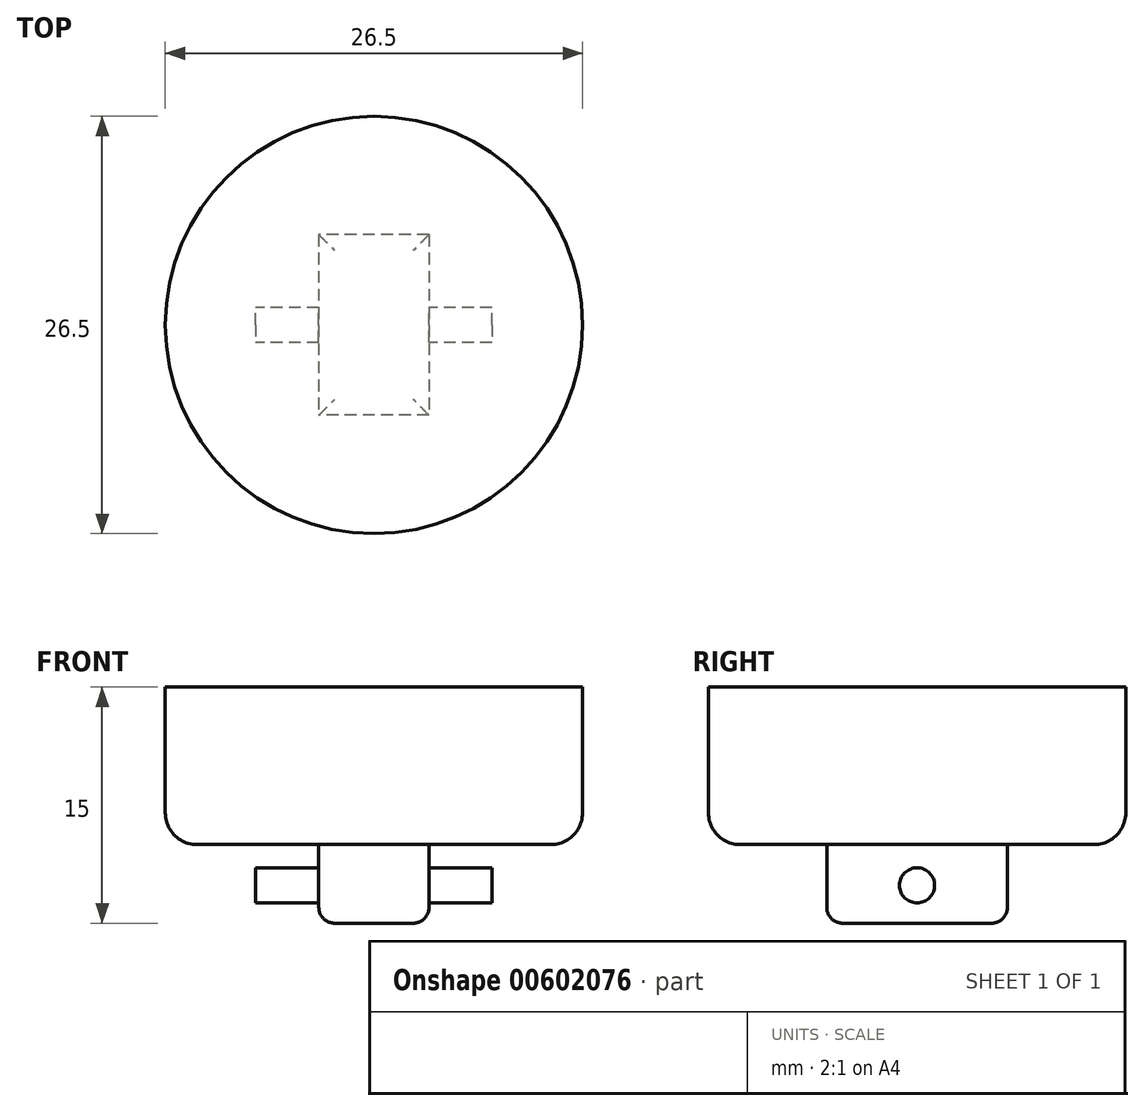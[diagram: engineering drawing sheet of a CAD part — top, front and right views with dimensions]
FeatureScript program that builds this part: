
annotation { "Feature Type Name" : "Feature", "Feature Type Description" : "" }
export const myFeature = defineFeature(function(context is Context, id is Id, definition is map)
    precondition{}
    {
        {
            var Q0;
            Q0=qCreatedBy(makeId("Top.planeOp"),FACE);
            var sketch = newSketch(context, id + "F0", { "sketchPlane" : qUnion([Q0])});
            skCircle(sketch, "E0", {"center": v(0, 0) * mm, "radius": 13.25 * mm});
            skSolve(sketch);
        }
        {
            var Q0;
            Q0 = qSketchRegion(id + "F0", true);
            extrude(context, id + "F1", {"entities" : qUnion([Q0]), "depth" : 10 * mm, "offsetDistance" : 25 * mm});
        }
        {
            var Q0;
            Q0=makeQuery(id+"F1.opExtrude","CAP_FACE",FACE,{"disambiguationData":[OSD([sQuery(id+"F0.wireOp",EDGE,"E0")])],"isStart":true});
            var sketch = newSketch(context, id + "F2", { "sketchPlane" : qUnion([Q0])});
            skLineSegment(sketch, "E1.bottom", {"start": v(3.5, -5.73) * mm, "end": v(-3.5, -5.73) * mm});
            skLineSegment(sketch, "E1.top", {"start": v(3.5, 5.73) * mm, "end": v(-3.5, 5.73) * mm});
            skLineSegment(sketch, "E1.left", {"start": v(3.5, -5.73) * mm, "end": v(3.5, 5.73) * mm});
            skLineSegment(sketch, "E1.right", {"start": v(-3.5, -5.73) * mm, "end": v(-3.5, 5.73) * mm});
            skPoint(sketch, "E1.middle", {"position": v(0, 0) * mm});
            skSolve(sketch);
        }
        {
            var Q0;
            Q0 = qSketchRegion(id + "F2", true);
            extrude(context, id + "F3", {"entities" : qUnion([Q0]), "operationType" : NewBodyOperationType.ADD, "depth" : 5 * mm, "offsetDistance" : 25 * mm});
        }
        {
            var Q0;
            Q0=qCreatedBy(makeId("Right.planeOp"),FACE);
            var sketch = newSketch(context, id + "F4", { "sketchPlane" : qUnion([Q0])});
            skCircle(sketch, "E2", {"center": v(0, -2.6) * mm, "radius": 1.12 * mm});
            skSolve(sketch);
        }
        {
            var Q0;
            Q0 = qSketchRegion(id + "F4", true);
            extrude(context, id + "F5", {"entities" : qUnion([Q0]), "operationType" : NewBodyOperationType.ADD, "depth" : 15 * mm, "offsetDistance" : 25 * mm, "symmetric" : true});
        }
        {
            var Q0;
            Q0=makeQuery(id+"F1.opExtrude","CAP_EDGE",EDGE,{"disambiguationData":[OSD([sQuery(id+"F0.wireOp",EDGE,"E0")])],"isStart":true});
            fillet(context, id + "F6", {"entities" : qUnion([Q0]), "radius" : 2 * mm, "tangentPropagation" : true, "allowEdgeOverflow" : false});
        }
        {
            var Q0;
            Q0=makeQuery(id+"F3.opExtrude","CAP_FACE",FACE,{"disambiguationData":[OSD([sQuery(id+"F2.wireOp",EDGE,"E1.bottom"),sQuery(id+"F2.wireOp",EDGE,"E1.top"),sQuery(id+"F2.wireOp",EDGE,"E1.left"),sQuery(id+"F2.wireOp",EDGE,"E1.right")])],"isStart":false});
            fillet(context, id + "F7", {"entities" : qUnion([Q0]), "radius" : 1 * mm, "tangentPropagation" : true, "allowEdgeOverflow" : false});
        }
    });
